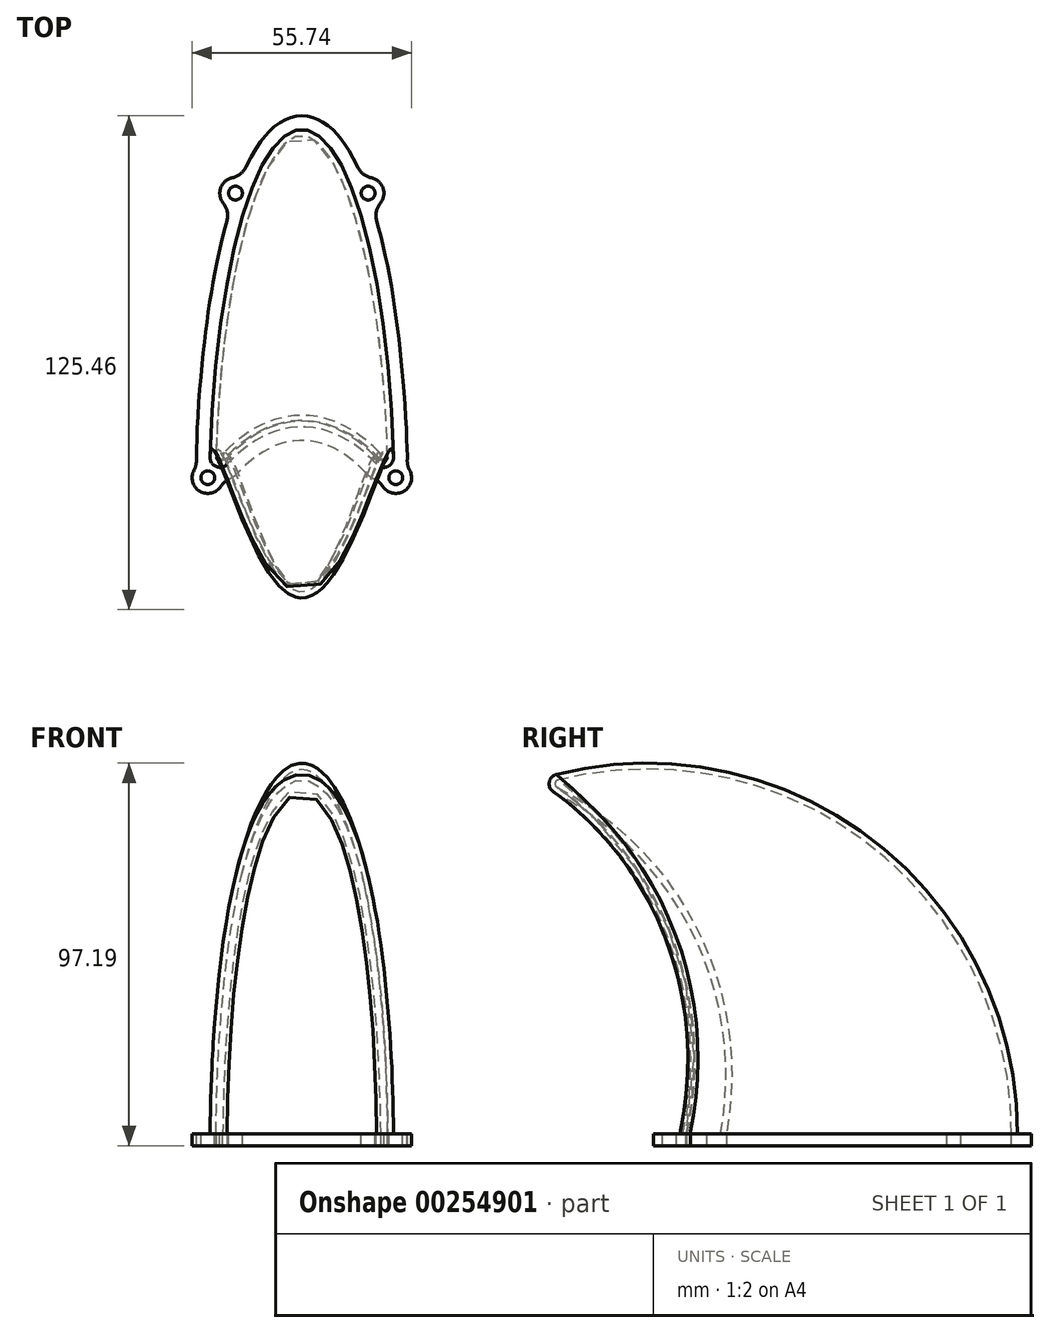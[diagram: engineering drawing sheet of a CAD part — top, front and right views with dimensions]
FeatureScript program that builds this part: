
annotation { "Feature Type Name" : "Feature", "Feature Type Description" : "" }
export const myFeature = defineFeature(function(context is Context, id is Id, definition is map)
    precondition{}
    {
        {
            var Q0;
            Q0=qCreatedBy(makeId("Top.planeOp"),FACE);
            var sketch = newSketch(context, id + "F0", { "sketchPlane" : qUnion([Q0])});
            skEllipticalArc(sketch, "E0", {});
            skLineSegment(sketch, "E1", {"start": v(-23.46, 0) * mm, "end": v(23.46, 0) * mm});
            const initialGuessF0  = {"E0": [0, 0, 0, 1, 0.09419305796368573, 0.023457994684576988, 4.71238898038469, 1.5707963267948966]};
            skSetInitialGuess(sketch, initialGuessF0);
            skSolve(sketch);
        }
        {
            var Q0;
            Q0=qCreatedBy(makeId("Top.planeOp"),FACE);
            var sketch = newSketch(context, id + "F1", { "sketchPlane" : qUnion([Q0])});
            skEllipticalArc(sketch, "E2", {});
            skLineSegment(sketch, "E3", {"start": v(-40.68, -140.7) * mm, "end": v(40.68, -140.7) * mm});
            const initialGuessF1  = {"E2": [0, -0.14069192111492157, 0, 1, 0.08080634676819629, 0.04068115038200901, 4.71238898038469, 1.5707963267948966]};
            skSetInitialGuess(sketch, initialGuessF1);
            skSolve(sketch);
        }
        {
            var Q0;
            Q0=makeQuery(id+"F0.imprint","IMPRINT",FACE,{"disambiguationData":[TD([[makeQuery(id+"F0.imprint","IMPRINT",EDGE,{"derivedFrom":sQuery(id+"F0.wireOp",EDGE,"E0")}),1.0]])]});
            var Q1;
            Q1=sQuery(id+"F0.wireOp",EDGE,"E1");
            revolve(context, id + "F2", {"entities" : qUnion([Q0]), "axis" : qUnion([Q1]), "revolveType" : RevolveType.ONE_DIRECTION, "angle" : 180 * degree});
        }
        {
            var Q0;
            Q0=makeQuery(id+"F1.imprint","IMPRINT",FACE,{"disambiguationData":[TD([[makeQuery(id+"F1.imprint","IMPRINT",EDGE,{"derivedFrom":sQuery(id+"F1.wireOp",EDGE,"E2")}),1.0]])]});
            var Q1;
            Q1=sQuery(id+"F1.wireOp",EDGE,"E3");
            revolve(context, id + "F3", {"entities" : qUnion([Q0]), "axis" : qUnion([Q1]), "revolveType" : RevolveType.FULL});
        }
        {
            var Q0;
            Q0=makeQuery(id+"F3.opRevolve","SWEPT_BODY",BODY,{"disambiguationData":[OSD([sQuery(id+"F1.wireOp",EDGE,"E2"),sQuery(id+"F1.wireOp",EDGE,"E3")])]});
            transform(context, id + "F4", {"entities" : qUnion([Q0]), "transformType" : TransformType.TRANSLATION_3D, "dx" : 0 * mm, "dy" : 80 * mm, "dz" : 15 * mm, "makeCopy" : false});
        }
        {
            var Q0;
            Q0=makeQuery(id+"F3.opRevolve","SWEPT_BODY",BODY,{"disambiguationData":[OSD([sQuery(id+"F1.wireOp",EDGE,"E2"),sQuery(id+"F1.wireOp",EDGE,"E3")])]});
            var Q1;
            Q1=makeQuery(id+"F2.opRevolve","SWEPT_BODY",BODY,{"disambiguationData":[OSD([sQuery(id+"F0.wireOp",EDGE,"E0"),sQuery(id+"F0.wireOp",EDGE,"E1")])]});
            booleanBodies(context, id + "F5", {"operationType" : BooleanOperationType.SUBTRACTION, "tools" : qUnion([Q0]), "targets" : qUnion([Q1])});
        }
        {
            var Q0;
            Q0=makeQuery(id+"F5.opBoolean","INTERSECT",EDGE,{"derivedFrom":[makeQuery(id+"F2.opRevolve","SWEPT_FACE",FACE,{"disambiguationData":[OSD([sQuery(id+"F0.wireOp",EDGE,"E0")])]}),makeQuery(id+"F3.opRevolve","SWEPT_FACE",FACE,{"disambiguationData":[OSD([sQuery(id+"F1.wireOp",EDGE,"E2")])]})]});
            fillet(context, id + "F6", {"entities" : qUnion([Q0]), "radius" : 2.5 * mm, "tangentPropagation" : true, "allowEdgeOverflow" : false});
        }
        {
            var Q0;
            Q0=makeQuery(id+"F2.opRevolve","CAP_FACE",FACE,{"disambiguationData":[OSD([sQuery(id+"F0.wireOp",EDGE,"E0"),sQuery(id+"F0.wireOp",EDGE,"E1")])],"isStart":false});
            shell(context, id + "F7", {"entities" : qUnion([Q0]), "thickness" : 1.5 * mm});
        }
        {
            var Q0;
            Q0=qCreatedBy(makeId("Top.planeOp"),FACE);
            var sketch = newSketch(context, id + "F8", { "sketchPlane" : qUnion([Q0])});
            skFitSpline(sketch, "E4.0", {"points": [v(21.8, 10.97) * mm, v(21.7, 14.64) * mm, v(21.45, 20.13) * mm, v(20.95, 27.44) * mm, v(20.33, 34.75) * mm, v(19.53, 42.03) * mm, v(18.5, 49.27) * mm, v(17.6, 54.69) * mm, v(16.56, 60.08) * mm, v(15.56, 64.55) * mm, v(14.66, 68.1) * mm, v(13.7, 71.65) * mm, v(12.6, 75.14) * mm, v(11.35, 78.58) * mm, v(10.31, 81.12) * mm, v(9.16, 83.62) * mm, v(7.85, 86.06) * mm, v(6.6, 88) * mm, v(5.6, 89.26) * mm, v(4.99, 89.96) * mm, v(4.5, 90.45) * mm, v(4, 90.92) * mm, v(3.46, 91.37) * mm, v(2.89, 91.76) * mm, v(2.3, 92.1) * mm, v(1.67, 92.4) * mm, v(1, 92.6) * mm, v(0.42, 92.68) * mm, v(-0.04, 92.7) * mm, v(-0.5, 92.67) * mm, v(-1.08, 92.58) * mm, v(-1.74, 92.36) * mm, v(-2.38, 92.07) * mm, v(-2.97, 91.71) * mm, v(-3.53, 91.3) * mm, v(-4.25, 90.7) * mm, v(-5.06, 89.9) * mm, v(-5.95, 88.84) * mm, v(-6.76, 87.72) * mm, v(-7.52, 86.56) * mm, v(-8.44, 84.98) * mm, v(-9.48, 82.95) * mm, v(-10.6, 80.45) * mm, v(-11.6, 77.9) * mm, v(-12.52, 75.32) * mm, v(-13.36, 72.7) * mm, v(-14.38, 69.2) * mm, v(-15.52, 64.8) * mm, v(-16.68, 59.5) * mm, v(-17.7, 54.16) * mm, v(-18.57, 48.82) * mm, v(-19.32, 43.45) * mm, v(-19.96, 38.07) * mm, v(-20.7, 30.88) * mm, v(-21.37, 21.86) * mm, v(-21.7, 14.6) * mm, v(-21.8, 10.97) * mm]});
            skFitSpline(sketch, "E5.0", {"points": [v(21.8, 10.97) * mm, v(21.8, 10.87) * mm, v(21.78, 10.67) * mm, v(21.62, 10.3) * mm, v(21.22, 9.94) * mm, v(20.58, 9.88) * mm, v(20.21, 10.09) * mm, v(20.08, 10.24) * mm]});
            skPoint(sketch, "E5.1", {"position": v(21.2, 10) * mm});
            skFitSpline(sketch, "E6.0", {"points": [v(20.08, 10.24) * mm, v(19.42, 10.94) * mm, v(18.06, 12.3) * mm, v(15.9, 14.18) * mm, v(13.6, 15.88) * mm, v(11.54, 17.12) * mm, v(9.8, 18) * mm, v(8.04, 18.76) * mm, v(6.22, 19.37) * mm, v(4.35, 19.81) * mm, v(2.9, 20.06) * mm, v(1.46, 20.2) * mm, v(-0.46, 20.27) * mm, v(-2.37, 20.14) * mm, v(-4.27, 19.83) * mm, v(-6.17, 19.39) * mm, v(-8.45, 18.62) * mm, v(-10.63, 17.6) * mm, v(-12.32, 16.65) * mm, v(-13.95, 15.62) * mm, v(-15.88, 14.2) * mm, v(-18.05, 12.31) * mm, v(-19.42, 10.94) * mm, v(-20.08, 10.24) * mm]});
            skFitSpline(sketch, "E7.0", {"points": [v(-20.08, 10.24) * mm, v(-20.15, 10.16) * mm, v(-20.3, 10.04) * mm, v(-20.6, 9.93) * mm, v(-20.9, 9.9) * mm, v(-21.3, 10.01) * mm, v(-21.7, 10.36) * mm, v(-21.8, 10.77) * mm, v(-21.8, 10.97) * mm]});
            skFitSpline(sketch, "E8.0", {"points": [v(16.42, 6.83) * mm, v(15.83, 7.45) * mm, v(14.64, 8.65) * mm, v(12.76, 10.28) * mm, v(10.8, 11.72) * mm, v(9.1, 12.75) * mm, v(7.68, 13.46) * mm, v(6.26, 14.08) * mm, v(4.81, 14.57) * mm, v(3.35, 14.9) * mm, v(2.24, 15.1) * mm, v(1.12, 15.21) * mm, v(-0.35, 15.26) * mm, v(-1.82, 15.16) * mm, v(-3.3, 14.92) * mm, v(-4.78, 14.58) * mm, v(-6.58, 13.97) * mm, v(-8.35, 13.15) * mm, v(-9.75, 12.36) * mm, v(-11.1, 11.5) * mm, v(-12.75, 10.3) * mm, v(-14.63, 8.66) * mm, v(-15.83, 7.45) * mm, v(-16.42, 6.83) * mm]});
            skFitSpline(sketch, "E9.0", {"points": [v(26.8, 11.12) * mm, v(26.8, 10.83) * mm, v(26.78, 10.24) * mm, v(26.61, 9.37) * mm, v(26.37, 8.68) * mm, v(26.12, 8.15) * mm, v(25.9, 7.75) * mm, v(25.64, 7.38) * mm, v(25.27, 6.9) * mm, v(24.75, 6.38) * mm, v(24.14, 5.93) * mm, v(23.61, 5.62) * mm, v(23.19, 5.4) * mm, v(22.74, 5.24) * mm, v(22.15, 5.06) * mm, v(21.4, 4.93) * mm, v(20.64, 4.9) * mm, v(20.03, 4.96) * mm, v(19.56, 5.04) * mm, v(19.1, 5.16) * mm, v(18.52, 5.36) * mm, v(17.83, 5.68) * mm, v(17.08, 6.19) * mm, v(16.63, 6.6) * mm, v(16.42, 6.83) * mm]});
            skFitSpline(sketch, "E9.1", {"points": [v(26.8, 11.12) * mm, v(26.69, 14.83) * mm, v(26.44, 20.4) * mm, v(25.94, 27.82) * mm, v(25.47, 33.39) * mm, v(24.9, 38.95) * mm, v(24.23, 44.5) * mm, v(23.44, 50.03) * mm, v(22.52, 55.56) * mm, v(21.46, 61.1) * mm, v(20.43, 65.7) * mm, v(19.5, 69.38) * mm, v(18.74, 72.14) * mm, v(17.92, 74.89) * mm, v(17.01, 77.63) * mm, v(16.02, 80.37) * mm, v(14.9, 83.1) * mm, v(13.85, 85.39) * mm, v(12.9, 87.22) * mm, v(12.13, 88.59) * mm, v(11.43, 89.72) * mm, v(10.82, 90.64) * mm, v(10.33, 91.31) * mm, v(9.81, 92) * mm, v(9.26, 92.68) * mm, v(8.66, 93.35) * mm, v(8, 94.03) * mm, v(7.29, 94.7) * mm, v(6.5, 95.34) * mm, v(5.75, 95.87) * mm, v(5.1, 96.27) * mm, v(4.58, 96.55) * mm, v(4.03, 96.82) * mm, v(3.42, 97.06) * mm, v(2.79, 97.28) * mm, v(2.1, 97.46) * mm, v(1.4, 97.6) * mm, v(0.66, 97.68) * mm, v(-0.09, 97.7) * mm, v(-0.84, 97.67) * mm, v(-1.57, 97.57) * mm, v(-2.28, 97.42) * mm, v(-2.94, 97.23) * mm, v(-3.58, 97) * mm, v(-4.17, 96.75) * mm, v(-4.9, 96.38) * mm, v(-5.73, 95.89) * mm, v(-6.6, 95.25) * mm, v(-7.4, 94.6) * mm, v(-8.1, 93.93) * mm, v(-8.74, 93.26) * mm, v(-9.33, 92.59) * mm, v(-10.06, 91.68) * mm, v(-10.9, 90.54) * mm, v(-11.78, 89.18) * mm, v(-12.84, 87.36) * mm, v(-14, 85.1) * mm, v(-15.21, 82.38) * mm, v(-16.29, 79.66) * mm, v(-17.26, 76.92) * mm, v(-18.14, 74.17) * mm, v(-18.94, 71.43) * mm, v(-19.68, 68.69) * mm, v(-20.58, 65.04) * mm, v(-21.58, 60.5) * mm, v(-22.62, 55.03) * mm, v(-23.5, 49.57) * mm, v(-24.28, 44.1) * mm, v(-24.93, 38.62) * mm, v(-25.67, 31.3) * mm, v(-26.36, 22.15) * mm, v(-26.69, 14.8) * mm, v(-26.8, 11.12) * mm]});
            skFitSpline(sketch, "E10.0", {"points": [v(-16.42, 6.83) * mm, v(-16.62, 6.6) * mm, v(-17.07, 6.2) * mm, v(-17.83, 5.68) * mm, v(-18.52, 5.36) * mm, v(-19.1, 5.16) * mm, v(-19.55, 5.05) * mm, v(-20, 4.97) * mm, v(-20.47, 4.92) * mm, v(-20.93, 4.92) * mm, v(-21.4, 4.94) * mm, v(-21.86, 5) * mm, v(-22.3, 5.1) * mm, v(-22.75, 5.24) * mm, v(-23.2, 5.41) * mm, v(-23.62, 5.62) * mm, v(-24.14, 5.93) * mm, v(-24.74, 6.37) * mm, v(-25.26, 6.9) * mm, v(-25.63, 7.37) * mm, v(-25.89, 7.74) * mm, v(-26.11, 8.14) * mm, v(-26.37, 8.68) * mm, v(-26.61, 9.37) * mm, v(-26.78, 10.23) * mm, v(-26.8, 10.82) * mm, v(-26.8, 11.12) * mm]});
            skCircle(sketch, "E11", {"center": v(23.87, 5.77) * mm, "radius": 4 * mm});
            skCircle(sketch, "E12", {"center": v(16.85, 78.06) * mm, "radius": 4 * mm});
            skCircle(sketch, "E13.MirrorC", {"center": v(-23.87, 5.77) * mm, "radius": 4 * mm});
            skCircle(sketch, "E14.MirrorC", {"center": v(-16.85, 78.06) * mm, "radius": 4 * mm});
            skCircle(sketch, "E15", {"center": v(-23.87, 5.77) * mm, "radius": 1.75 * mm});
            skCircle(sketch, "E16", {"center": v(-16.85, 78.06) * mm, "radius": 1.75 * mm});
            skCircle(sketch, "E17.MirrorC", {"center": v(16.85, 78.06) * mm, "radius": 1.75 * mm});
            skCircle(sketch, "E18.MirrorC", {"center": v(23.87, 5.77) * mm, "radius": 1.75 * mm});
            skSolve(sketch);
        }
        {
            var Q0;
            Q0 = qSketchRegion(id + "F8", true);
            extrude(context, id + "F9", {"entities" : qUnion([Q0]), "operationType" : NewBodyOperationType.ADD, "oppositeDirection" : true, "depth" : 3 * mm});
        }
        {
            var Q0;
            {var subQ0=sQuery(id+"F8.wireOp",EDGE,"E13.MirrorC");var subQ1=sQuery(id+"F8.wireOp",EDGE,"E10.0");Q0=makeQuery(id+"F9.opExtrude","SWEPT_EDGE",EDGE,{"disambiguationData":[OSD([subQ1,subQ0]),TDD([makeQuery(id+"F8.imprint","INTERSECT",VERTEX,{"disambiguationData":[OD(1.0)],"derivedFrom":[subQ1,subQ0]})])]});}
            var Q1;
            {var subQ0=sQuery(id+"F8.wireOp",EDGE,"E11");var subQ1=sQuery(id+"F8.wireOp",EDGE,"E9.0");Q1=makeQuery(id+"F9.opExtrude","SWEPT_EDGE",EDGE,{"disambiguationData":[OSD([subQ1,subQ0]),TDD([makeQuery(id+"F8.imprint","INTERSECT",VERTEX,{"disambiguationData":[OD(0.0)],"derivedFrom":[subQ1,subQ0]})])]});}
            var Q2;
            {var subQ0=sQuery(id+"F8.wireOp",EDGE,"E11");var subQ1=sQuery(id+"F8.wireOp",EDGE,"E9.0");Q2=makeQuery(id+"F9.opExtrude","SWEPT_EDGE",EDGE,{"disambiguationData":[OSD([subQ1,subQ0]),TDD([makeQuery(id+"F8.imprint","INTERSECT",VERTEX,{"disambiguationData":[OD(1.0)],"derivedFrom":[subQ1,subQ0]})])]});}
            var Q3;
            {var subQ0=sQuery(id+"F8.wireOp",EDGE,"E13.MirrorC");var subQ1=sQuery(id+"F8.wireOp",EDGE,"E10.0");Q3=makeQuery(id+"F9.opExtrude","SWEPT_EDGE",EDGE,{"disambiguationData":[OSD([subQ1,subQ0]),TDD([makeQuery(id+"F8.imprint","INTERSECT",VERTEX,{"disambiguationData":[OD(0.0)],"derivedFrom":[subQ1,subQ0]})])]});}
            var Q4;
            {var subQ0=sQuery(id+"F8.wireOp",EDGE,"E12");var subQ1=sQuery(id+"F8.wireOp",EDGE,"E9.1");Q4=makeQuery(id+"F9.opExtrude","SWEPT_EDGE",EDGE,{"disambiguationData":[OSD([subQ1,subQ0]),TDD([makeQuery(id+"F8.imprint","INTERSECT",VERTEX,{"disambiguationData":[OD(0.0)],"derivedFrom":[subQ1,subQ0]})])]});}
            var Q5;
            {var subQ0=sQuery(id+"F8.wireOp",EDGE,"E12");var subQ1=sQuery(id+"F8.wireOp",EDGE,"E9.1");Q5=makeQuery(id+"F9.opExtrude","SWEPT_EDGE",EDGE,{"disambiguationData":[OSD([subQ1,subQ0]),TDD([makeQuery(id+"F8.imprint","INTERSECT",VERTEX,{"disambiguationData":[OD(1.0)],"derivedFrom":[subQ1,subQ0]})])]});}
            var Q6;
            {var subQ0=sQuery(id+"F8.wireOp",EDGE,"E14.MirrorC");var subQ1=sQuery(id+"F8.wireOp",EDGE,"E9.1");Q6=makeQuery(id+"F9.opExtrude","SWEPT_EDGE",EDGE,{"disambiguationData":[OSD([subQ1,subQ0]),TDD([makeQuery(id+"F8.imprint","INTERSECT",VERTEX,{"disambiguationData":[OD(0.0)],"derivedFrom":[subQ1,subQ0]})])]});}
            var Q7;
            {var subQ0=sQuery(id+"F8.wireOp",EDGE,"E14.MirrorC");var subQ1=sQuery(id+"F8.wireOp",EDGE,"E9.1");Q7=makeQuery(id+"F9.opExtrude","SWEPT_EDGE",EDGE,{"disambiguationData":[OSD([subQ1,subQ0]),TDD([makeQuery(id+"F8.imprint","INTERSECT",VERTEX,{"disambiguationData":[OD(1.0)],"derivedFrom":[subQ1,subQ0]})])]});}
            fillet(context, id + "F10", {"entities" : qUnion([Q0, Q1, Q2, Q3, Q4, Q5, Q6, Q7]), "radius" : 5 * mm, "tangentPropagation" : true, "allowEdgeOverflow" : false});
        }
    });
